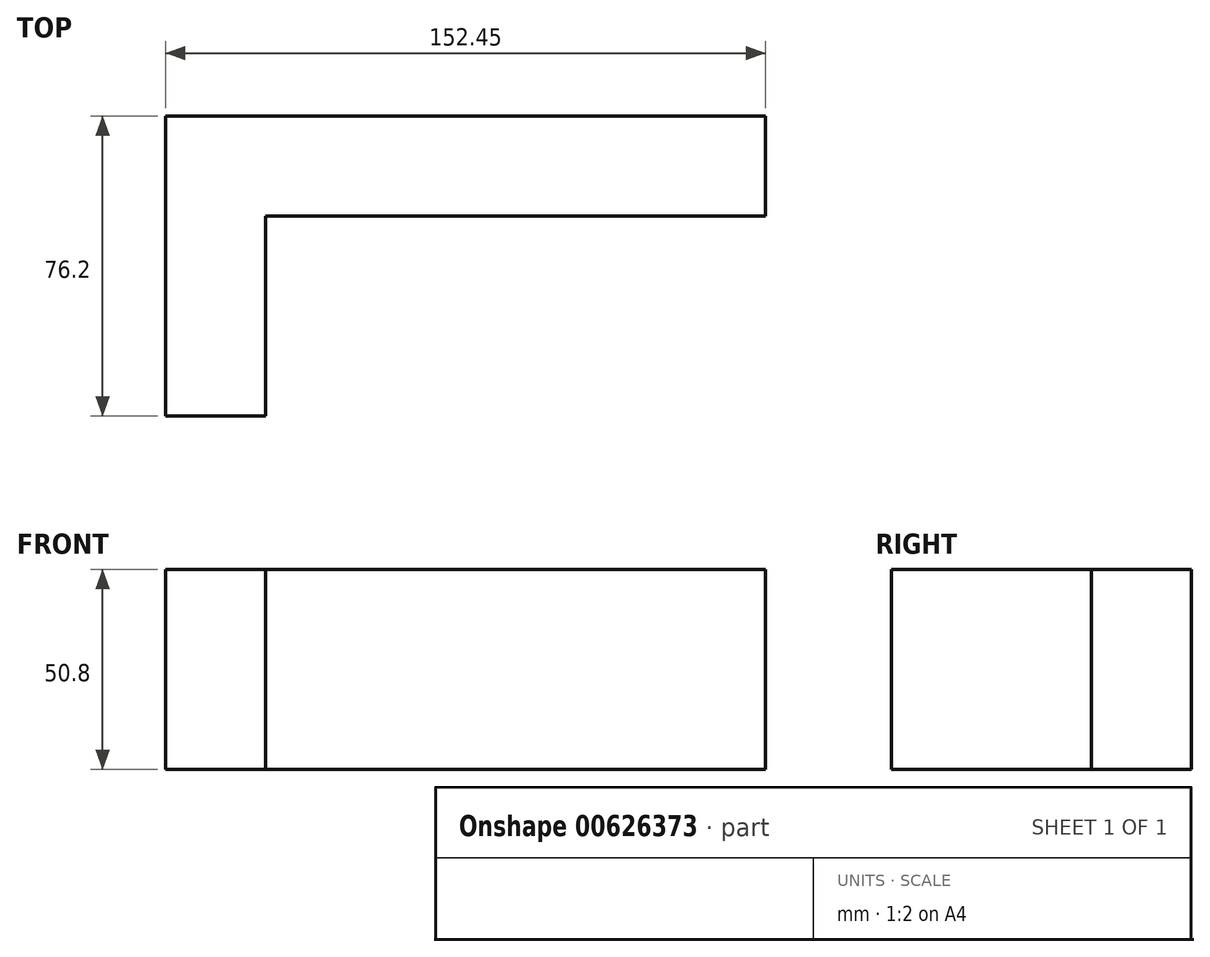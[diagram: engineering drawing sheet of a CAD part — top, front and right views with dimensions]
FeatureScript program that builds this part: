
annotation { "Feature Type Name" : "Feature", "Feature Type Description" : "" }
export const myFeature = defineFeature(function(context is Context, id is Id, definition is map)
    precondition{}
    {
        {
            var Q0;
            Q0=qCreatedBy(makeId("Top.planeOp"),FACE);
            var sketch = newSketch(context, id + "F0", { "sketchPlane" : qUnion([Q0])});
            skLineSegment(sketch, "E0", {"start": v(229.52, -52.2) * mm, "end": v(229.52, 24) * mm});
            skLineSegment(sketch, "E1", {"start": v(229.52, 24) * mm, "end": v(381.92, 24) * mm});
            skLineSegment(sketch, "E2", {"start": v(229.52, -52.2) * mm, "end": v(254.92, -52.2) * mm});
            skLineSegment(sketch, "E3", {"start": v(254.92, -52.2) * mm, "end": v(254.92, -1.4) * mm});
            skLineSegment(sketch, "E4", {"start": v(254.92, -1.4) * mm, "end": v(381.97, -1.4) * mm});
            skLineSegment(sketch, "E5", {"start": v(381.97, -1.4) * mm, "end": v(381.92, 24) * mm});
            skSolve(sketch);
        }
        {
            var Q0;
            Q0=makeQuery(id+"F0.imprint","IMPRINT",FACE,{"disambiguationData":[TD([[makeQuery(id+"F0.imprint","IMPRINT",EDGE,{"derivedFrom":sQuery(id+"F0.wireOp",EDGE,"E0")}),-1.0]])]});
            extrude(context, id + "F1", {"entities" : qUnion([Q0]), "depth" : 50.8 * mm, "offsetDistance" : 25.4 * mm});
        }
    });
